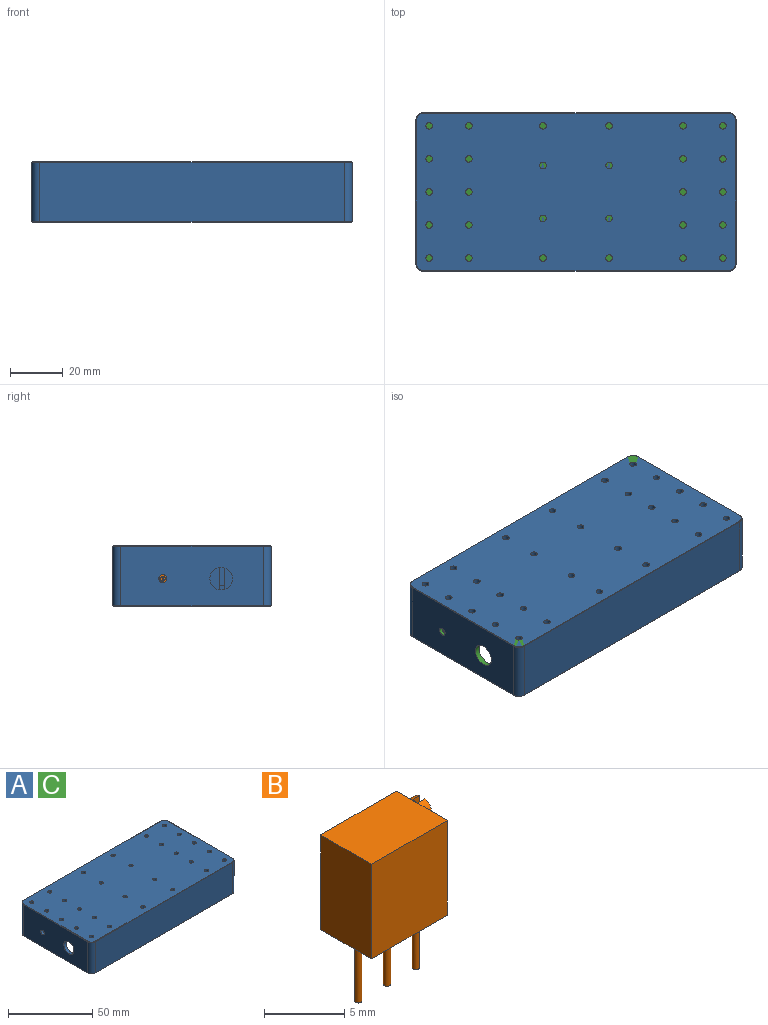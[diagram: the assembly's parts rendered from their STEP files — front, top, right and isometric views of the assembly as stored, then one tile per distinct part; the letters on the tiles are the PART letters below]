
ASSEMBLY  parts=3 mates=1
PART A: 148 faces, bbox 121x60x23 mm
  f0: cone r=2.8mm half-angle=45deg, axis (0,0,-1), area 1.3mm2, adj f22,f43,f44,f113
  f1: plane 54x0.2mm, normal (0.71,0,0.71), area 15.3mm2, adj f2,f10,f42,f113
  f2: cone r=2.8mm half-angle=45deg, axis (0,0,-1), area 1.3mm2, adj f1,f25,f44,f113
  f3: plane 115.5x53mm, normal (0,0,-1), area 5729.7mm2, adj f4,f5,f6,f7,f8,f14,f15,f16
  f4: plane 14x6.7mm, normal (-1,0,0), area 93.8mm2, adj f3,f29,f116,f146
  f5: plane 49x9mm, normal (-1,0,0), area 441mm2, adj f3,f16,f17,f142
  f6: plane 93x9mm, normal (0,1,0), area 837mm2, adj f3,f15,f16,f142
  f7: plane 12.2x9mm, normal (1,0,0), area 109.8mm2, adj f3,f15,f116,f142
  f8: plane 93x9mm, normal (0,-1,0), area 837mm2, adj f3,f14,f17,f142
  f9: plane 120.6x59.6mm, normal (0,0,-1), area 632.5mm2, adj f18,f19,f20,f21,f32,f33,f34,f35
  f10: plane 54x22.6mm, normal (1,0,0), area 1220.4mm2, adj f1,f24,f25,f36
  f11: plane 115x22.6mm, normal (0,-1,0), area 2599mm2, adj f23,f24,f32,f40
  f12: plane 54x22.6mm, normal (-1,0,0), area 1156.6mm2, adj f22,f23,f35,f43,f114,f115
  f13: plane 115x22.6mm, normal (0,1,0), area 2599mm2, adj f22,f25,f39,f44
  f14: cylinder r=2mm len=9mm, axis (0,0,1), area 28.3mm2, adj f3,f8,f140,f142
  f15: cylinder r=2mm len=9mm, axis (0,0,-1), area 28.3mm2, adj f3,f6,f7,f142
  f16: cylinder r=2mm len=9mm, axis (0,0,1), area 28.3mm2, adj f3,f5,f6,f142
  f17: cylinder r=2mm len=9mm, axis (0,0,-1), area 28.3mm2, adj f3,f5,f8,f142
  f18: cylinder r=2mm len=3mm, axis (0,0,1), area 9.4mm2, adj f9,f143,f146,f147
  f19: cylinder r=2mm len=3mm, axis (0,0,-1), area 9.4mm2, adj f9,f138,f145,f147
  f20: cylinder r=2mm len=8mm, axis (0,0,1), area 25.1mm2, adj f9,f133,f142,f145
  f21: cylinder r=2mm len=8mm, axis (0,0,-1), area 25.1mm2, adj f9,f133,f142,f143
  f22: cylinder r=3mm len=22.6mm, axis (0,0,-1), area 106.5mm2, adj f0,f12,f13,f37
  f23: cylinder r=3mm len=22.6mm, axis (0,0,1), area 106.5mm2, adj f11,f12,f33,f41
  f24: cylinder r=3mm len=22.6mm, axis (0,0,-1), area 106.5mm2, adj f10,f11,f34,f42
  f25: cylinder r=3mm len=22.6mm, axis (0,0,1), area 106.5mm2, adj f2,f10,f13,f38
  f26: cylinder r=1.5mm len=5mm, axis (0,0,-1), area 15.6mm2, adj f56,f142,f143,f146
  f27: cylinder r=1.5mm len=5mm, axis (0,0,-1), area 15.6mm2, adj f55,f138,f142,f145
  f28: cylinder r=2mm len=14mm, axis (0,0,1), area 44mm2, adj f3,f54,f146,f147
  f29: cylinder r=2mm len=14mm, axis (0,0,-1), area 44mm2, adj f3,f4,f54,f146
  f30: cylinder r=2mm len=14mm, axis (0,0,-1), area 44mm2, adj f3,f53,f138,f147
  f31: cylinder r=2mm len=14mm, axis (0,0,1), area 44mm2, adj f3,f53,f134,f138
  f32: plane 115x0.2mm, normal (0,-0.71,-0.71), area 32.5mm2, adj f9,f11,f33,f34
  f33: cone r=2.8mm half-angle=45deg, axis (0,0,1), area 1.3mm2, adj f9,f23,f32,f35
  f34: cone r=2.8mm half-angle=45deg, axis (0,0,1), area 1.3mm2, adj f9,f24,f32,f36
  f35: plane 54x0.2mm, normal (-0.71,0,-0.71), area 15.3mm2, adj f9,f12,f33,f37
  f36: plane 54x0.2mm, normal (0.71,0,-0.71), area 15.3mm2, adj f9,f10,f34,f38
  f37: cone r=2.8mm half-angle=45deg, axis (0,0,1), area 1.3mm2, adj f9,f22,f35,f39
  f38: cone r=2.8mm half-angle=45deg, axis (0,0,1), area 1.3mm2, adj f9,f25,f36,f39
  f39: plane 115x0.2mm, normal (0,0.71,-0.71), area 32.5mm2, adj f9,f13,f37,f38
  f40: plane 115x0.2mm, normal (0,-0.71,0.71), area 32.5mm2, adj f11,f41,f42,f113
  f41: cone r=2.8mm half-angle=45deg, axis (0,0,-1), area 1.3mm2, adj f23,f40,f43,f113
  f42: cone r=2.8mm half-angle=45deg, axis (0,0,-1), area 1.3mm2, adj f1,f24,f40,f113
  f43: plane 54x0.2mm, normal (-0.71,0,0.71), area 15.3mm2, adj f0,f12,f41,f113
  f44: plane 115x0.2mm, normal (0,0.71,0.71), area 32.5mm2, adj f0,f2,f13,f113
  f45: plane 2.5x2.5mm, normal (0,0,-1), area 4.9mm2, adj f46
  f46: cylinder r=1.25mm len=10mm, axis (0,0,1), area 78.5mm2, adj f45,f146
  f47: plane 2.5x2.5mm, normal (0,0,-1), area 4.9mm2, adj f48
  f48: cylinder r=1.25mm len=10mm, axis (0,0,1), area 78.5mm2, adj f47,f146
  f49: plane 2.5x2.5mm, normal (0,0,-1), area 4.9mm2, adj f50
  f50: cylinder r=1.25mm len=10mm, axis (0,0,1), area 78.5mm2, adj f49,f138
  f51: plane 2.5x2.5mm, normal (0,0,-1), area 4.9mm2, adj f52
  f52: cylinder r=1.25mm len=10mm, axis (0,0,1), area 78.5mm2, adj f51,f138
  f53: plane 14x10.5mm, normal (0,-1,0), area 147mm2, adj f3,f30,f31,f138
  f54: plane 14x10.5mm, normal (0,1,0), area 147mm2, adj f3,f28,f29,f146
  f55: plane 5x1.76mm, normal (0.87,0.49,0), area 10.1mm2, adj f27,f138,f142,f144
  f56: plane 5x1.76mm, normal (0.87,-0.49,0), area 10.1mm2, adj f26,f137,f142,f146
  f57: cylinder r=1.25mm len=5mm, axis (0,0,-1), area 39.3mm2, adj f58,f113
  f58: plane 2.5x2.5mm, normal (0,0,1), area 4.9mm2, adj f57
  f59: cylinder r=1.25mm len=5mm, axis (0,0,-1), area 39.3mm2, adj f60,f113
  f60: plane 2.5x2.5mm, normal (0,0,1), area 4.9mm2, adj f59
  f61: cylinder r=1.25mm len=5mm, axis (0,0,-1), area 39.3mm2, adj f62,f113
  f62: plane 2.5x2.5mm, normal (0,0,1), area 4.9mm2, adj f61
  f63: cylinder r=1.25mm len=5mm, axis (0,0,-1), area 39.3mm2, adj f64,f113
  f64: plane 2.5x2.5mm, normal (0,0,1), area 4.9mm2, adj f63
  f65: cylinder r=1.25mm len=5mm, axis (0,0,-1), area 39.3mm2, adj f66,f113
  f66: plane 2.5x2.5mm, normal (0,0,1), area 4.9mm2, adj f65
  f67: cylinder r=1.25mm len=5mm, axis (0,0,-1), area 39.3mm2, adj f68,f113
  f68: plane 2.5x2.5mm, normal (0,0,1), area 4.9mm2, adj f67
  f69: cylinder r=1.25mm len=5mm, axis (0,0,-1), area 39.3mm2, adj f70,f113
  f70: plane 2.5x2.5mm, normal (0,0,1), area 4.9mm2, adj f69
  f71: cylinder r=1.25mm len=5mm, axis (0,0,-1), area 39.3mm2, adj f72,f113
  f72: plane 2.5x2.5mm, normal (0,0,1), area 4.9mm2, adj f71
  f73: cylinder r=1.25mm len=5mm, axis (0,0,-1), area 39.3mm2, adj f74,f113
  f74: plane 2.5x2.5mm, normal (0,0,1), area 4.9mm2, adj f73
  f75: cylinder r=1.25mm len=5mm, axis (0,0,-1), area 39.3mm2, adj f76,f113
  f76: plane 2.5x2.5mm, normal (0,0,1), area 4.9mm2, adj f75
  f77: cylinder r=1.25mm len=5mm, axis (0,0,-1), area 39.3mm2, adj f78,f113
  f78: plane 2.5x2.5mm, normal (0,0,1), area 4.9mm2, adj f77
  f79: cylinder r=1.25mm len=5mm, axis (0,0,-1), area 39.3mm2, adj f80,f113
  f80: plane 2.5x2.5mm, normal (0,0,1), area 4.9mm2, adj f79
  f81: cylinder r=1.25mm len=5mm, axis (0,0,-1), area 39.3mm2, adj f82,f113
  f82: plane 2.5x2.5mm, normal (0,0,1), area 4.9mm2, adj f81
  f83: cylinder r=1.25mm len=5mm, axis (0,0,-1), area 39.3mm2, adj f84,f113
  f84: plane 2.5x2.5mm, normal (0,0,1), area 4.9mm2, adj f83
  f85: cylinder r=1.25mm len=5mm, axis (0,0,-1), area 39.3mm2, adj f86,f113
  f86: plane 2.5x2.5mm, normal (0,0,1), area 4.9mm2, adj f85
  f87: cylinder r=1.25mm len=5mm, axis (0,0,-1), area 39.3mm2, adj f88,f113
  f88: plane 2.5x2.5mm, normal (0,0,1), area 4.9mm2, adj f87
  f89: cylinder r=1.25mm len=5mm, axis (0,0,-1), area 39.3mm2, adj f90,f113
  f90: plane 2.5x2.5mm, normal (0,0,1), area 4.9mm2, adj f89
  f91: cylinder r=1.25mm len=5mm, axis (0,0,-1), area 39.3mm2, adj f92,f113
  f92: plane 2.5x2.5mm, normal (0,0,1), area 4.9mm2, adj f91
  f93: cylinder r=1.25mm len=5mm, axis (0,0,-1), area 39.3mm2, adj f94,f113
  f94: plane 2.5x2.5mm, normal (0,0,1), area 4.9mm2, adj f93
  f95: cylinder r=1.25mm len=5mm, axis (0,0,-1), area 39.3mm2, adj f96,f113
  f96: plane 2.5x2.5mm, normal (0,0,1), area 4.9mm2, adj f95
  f97: cylinder r=1.25mm len=5mm, axis (0,0,-1), area 39.3mm2, adj f98,f113
  f98: plane 2.5x2.5mm, normal (0,0,1), area 4.9mm2, adj f97
  f99: cylinder r=1.25mm len=5mm, axis (0,0,-1), area 39.3mm2, adj f100,f113
  f100: plane 2.5x2.5mm, normal (0,0,1), area 4.9mm2, adj f99
  f101: cylinder r=1.25mm len=5mm, axis (0,0,-1), area 39.3mm2, adj f102,f113
  f102: plane 2.5x2.5mm, normal (0,0,1), area 4.9mm2, adj f101
  f103: cylinder r=1.25mm len=5mm, axis (0,0,-1), area 39.3mm2, adj f104,f113
  f104: plane 2.5x2.5mm, normal (0,0,1), area 4.9mm2, adj f103
  f105: cylinder r=1.25mm len=5mm, axis (0,0,-1), area 39.3mm2, adj f106,f113
  f106: plane 2.5x2.5mm, normal (0,0,1), area 4.9mm2, adj f105
  f107: cylinder r=1.25mm len=5mm, axis (0,0,-1), area 39.3mm2, adj f108,f113
  f108: plane 2.5x2.5mm, normal (0,0,1), area 4.9mm2, adj f107
  f109: cylinder r=1.25mm len=5mm, axis (0,0,-1), area 39.3mm2, adj f110,f113
  f110: plane 2.5x2.5mm, normal (0,0,1), area 4.9mm2, adj f109
  f111: cylinder r=1.25mm len=5mm, axis (0,0,-1), area 39.3mm2, adj f112,f113
  f112: plane 2.5x2.5mm, normal (0,0,1), area 4.9mm2, adj f111
  f113: plane 120.6x59.6mm, normal (0,0,1), area 7043.6mm2, adj f0,f1,f2,f40,f41,f42,f43,f44
  f114: cylinder r=1.5mm len=3mm, axis (1,0,0), area 18.8mm2, adj f12,f147
  f115: cylinder r=4.25mm len=8.5mm, axis (1,0,0), area 53.4mm2, adj f12,f147
  f116: plane 14x4mm, normal (0,1,0), area 48.5mm2, adj f3,f4,f7,f137,f142,f146
  f117: plane 14x4mm, normal (0,-1,0), area 48.5mm2, adj f3,f132,f135,f136,f139,f141
  f118: plane 14x4mm, normal (0,1,0), area 48.5mm2, adj f3,f132,f135,f136,f139,f141
  f119: plane 14x4mm, normal (0,-1,0), area 48.5mm2, adj f3,f134,f138,f140,f142,f144
  f120: plane 2.5x2.5mm, normal (0,0,-1), area 4.9mm2, adj f121
  f121: cylinder r=1.25mm len=3mm, axis (0,0,1), area 23.6mm2, adj f3,f120
  f122: plane 2.5x2.5mm, normal (0,0,-1), area 4.9mm2, adj f123
  f123: cylinder r=1.25mm len=3mm, axis (0,0,1), area 23.6mm2, adj f3,f122
  f124: plane 2.5x2.5mm, normal (0,0,-1), area 4.9mm2, adj f125
  f125: cylinder r=1.25mm len=3mm, axis (0,0,1), area 23.6mm2, adj f3,f124
  f126: plane 2.5x2.5mm, normal (0,0,-1), area 4.9mm2, adj f127
  f127: cylinder r=1.25mm len=3mm, axis (0,0,1), area 23.6mm2, adj f3,f126
  f128: plane 2.5x2.5mm, normal (0,0,-1), area 4.9mm2, adj f129
  f129: cylinder r=1.25mm len=3mm, axis (0,0,1), area 23.6mm2, adj f3,f128
  f130: plane 2.5x2.5mm, normal (0,0,-1), area 4.9mm2, adj f131
  f131: cylinder r=1.25mm len=3mm, axis (0,0,1), area 23.6mm2, adj f3,f130
  f132: plane 20.6x1.5mm, normal (0,0,-1), area 30.9mm2, adj f117,f118,f136,f141
  f133: plane 52x8mm, normal (-1,0,0), area 416mm2, adj f9,f20,f21,f142
  f134: plane 14x6.7mm, normal (-1,0,0), area 93.8mm2, adj f3,f31,f119,f138
  f135: plane 20.6x14mm, normal (-1,0,0), area 288.4mm2, adj f3,f117,f118,f139
  f136: plane 20.6x5mm, normal (1,0,0), area 103mm2, adj f117,f118,f132,f139
  f137: plane 11.7x5mm, normal (1,0,0), area 58.5mm2, adj f56,f116,f142,f146
  f138: plane 17.31x15.7mm, normal (0,0,-1), area 128.8mm2, adj f19,f27,f30,f31,f50,f52,f53,f55
  f139: plane 20.6x2.5mm, normal (0,0,-1), area 51.5mm2, adj f117,f118,f135,f136
  f140: plane 12.2x9mm, normal (1,0,0), area 109.8mm2, adj f3,f14,f119,f142
  f141: plane 20.6x9mm, normal (1,0,0), area 185.4mm2, adj f3,f117,f118,f132
  f142: plane 101.19x56mm, normal (0,0,-1), area 429.8mm2, adj f5,f6,f7,f8,f14,f15,f16,f17
  f143: plane 113x8mm, normal (0,1,0), area 827.4mm2, adj f9,f18,f21,f26,f142,f146
  f144: plane 11.7x5mm, normal (1,0,0), area 58.5mm2, adj f55,f119,f138,f142
  f145: plane 113x8mm, normal (0,-1,0), area 827.4mm2, adj f9,f19,f20,f27,f138,f142
  f146: plane 17.31x15.7mm, normal (0,0,-1), area 128.8mm2, adj f4,f18,f26,f28,f29,f46,f48,f54
  f147: plane 52x17mm, normal (1,0,0), area 624.2mm2, adj f3,f9,f18,f19,f28,f30,f114,f115
PART B: 18 faces, bbox 7.7x4.5x12 mm
  f0: cylinder r=0.89mm len=1.78mm, axis (-1,0,0), area 5mm2, adj f1,f2,f5,f9,f10,f11
  f1: plane 1.71x0.64mm, normal (1,0,0), area 0.8mm2, adj f0,f10
  f2: plane 1.71x0.64mm, normal (1,0,0), area 0.8mm2, adj f0,f11
  f3: plane 7.24x4.5mm, normal (-1,0,0), area 32.6mm2, adj f4,f6,f7,f8
  f4: plane 7.24x6.71mm, normal (0,-1,0), area 48.6mm2, adj f3,f5,f7,f8
  f5: plane 7.24x4.5mm, normal (1,0,0), area 30.1mm2, adj f0,f4,f6,f7,f8
  f6: plane 7.24x6.71mm, normal (0,1,0), area 48.6mm2, adj f3,f5,f7,f8
  f7: plane 6.71x4.5mm, normal (0,0,1), area 30.2mm2, adj f3,f4,f5,f6
  f8: plane 6.71x4.5mm, normal (0,0,-1), area 29.7mm2, adj f3,f4,f5,f6,f12,f14,f16
  f9: plane 1.8x0.51mm, normal (1,0,0), area 0.9mm2, adj f0,f10,f11
  f10: plane 1.71x0.64mm, normal (0,-1,0), area 1.1mm2, adj f0,f1,f9
  f11: plane 1.71x0.64mm, normal (0,1,0), area 1.1mm2, adj f0,f2,f9
  f12: cylinder r=0.23mm len=4.78mm, axis (0,0,1), area 6.9mm2, adj f8,f13
  f13: plane 0.46x0.46mm, normal (0,0,-1), area 0.2mm2, adj f12
  f14: cylinder r=0.23mm len=4.78mm, axis (0,0,1), area 6.9mm2, adj f8,f15
  f15: plane 0.46x0.46mm, normal (0,0,-1), area 0.2mm2, adj f14
  f16: cylinder r=0.23mm len=4.78mm, axis (0,0,1), area 6.9mm2, adj f8,f17
  f17: plane 0.46x0.46mm, normal (0,0,-1), area 0.2mm2, adj f16
PART C: same geometry as A
PLACE A t=(-37.27,-15.2,5.34)mm
PLACE B rot(axis=(0,1,0),180deg) t=(-100.9,-5.21,21.86)mm
PLACE C t=(-37.27,-15.2,5.34)mm
MATE fastened B.f0 <-> A.f114  axis (-1,0,0) through (-105.27,-4.2,15.84)mm
